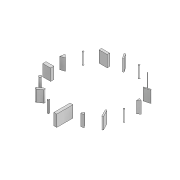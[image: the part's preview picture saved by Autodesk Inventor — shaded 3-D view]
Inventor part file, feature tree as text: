
AUTODESK INVENTOR PART (.ipt)
format: ipt  version: 2021 (Build 250183000, 183)  size: 157,184 bytes
history: native  units: in
note: dims shown in document units (in); Inventor stores cm internally (conversion verified against a paired STEP export)
features: extrude x1, sketch x1
ambient origin geometry x8: Origin, YZ Plane, XZ Plane, XY Plane, X Axis, Y Axis, Z Axis, Center Point
bodies: Solid1 (feature_tree)
feature tree (2):
  extrude  "Extrusion1"  Depth=118.1102in
  sketch  "Sketch1"  dims[d0=787.4016in d1=0.0773in d2=6.2992in d4=360.0deg d6=118.1102in d7=0.0in]
